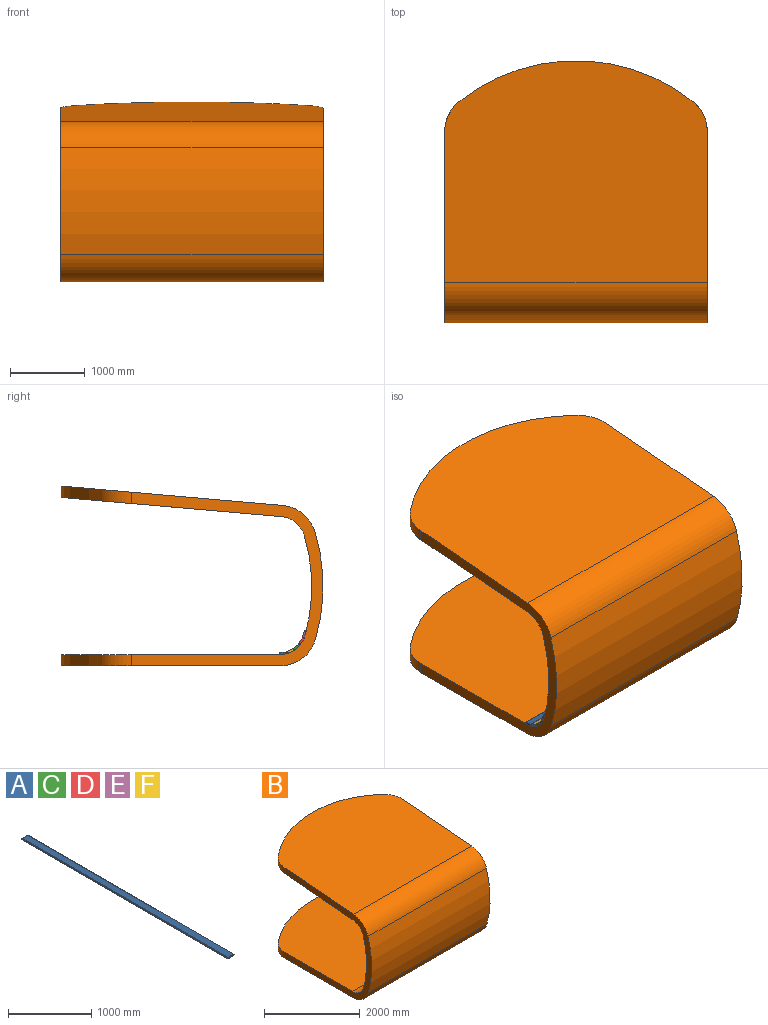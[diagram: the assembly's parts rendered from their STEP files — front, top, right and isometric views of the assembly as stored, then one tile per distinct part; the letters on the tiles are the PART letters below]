
ASSEMBLY  parts=6 mates=9
PART A: 14 faces, bbox 105x3500x25 mm
  f0: plane 3500x91mm, normal (0,0,1), area 318500mm2, adj f8,f9,f11,f13
  f1: plane 3500x1.84mm, normal (-1,0,0), area 6439.1mm2, adj f2,f8,f9,f13
  f2: cylinder r=10mm len=3500mm, axis (0,1,0), area 73303.8mm2, adj f1,f3,f8,f9
  f3: plane 3500x1.84mm, normal (-1,0,0), area 6439.1mm2, adj f2,f8,f9,f12
  f4: plane 3500x91mm, normal (0,0,-1), area 318500mm2, adj f8,f9,f10,f12
  f5: plane 3500x0.5mm, normal (1,0,0), area 1750mm2, adj f6,f8,f9,f10
  f6: cylinder r=10mm len=3500mm, axis (0,1,0), area 109955.7mm2, adj f5,f7,f8,f9
  f7: plane 3500x0.5mm, normal (1,0,0), area 1750mm2, adj f6,f8,f9,f11
  f8: plane 105x25mm, normal (0,-1,0), area 2462.7mm2, adj f0,f1,f2,f3,f4,f5,f6,f7
  f9: plane 105x25mm, normal (0,1,0), area 2462.7mm2, adj f0,f1,f2,f3,f4,f5,f6,f7
  f10: plane 3500x2mm, normal (0.71,0,-0.71), area 9899.5mm2, adj f4,f5,f8,f9
  f11: plane 3500x2mm, normal (0.71,0,0.71), area 9899.5mm2, adj f0,f7,f8,f9
  f12: plane 3500x2mm, normal (-0.71,0,-0.71), area 9899.5mm2, adj f3,f4,f8,f9
  f13: plane 3500x2mm, normal (-0.71,0,0.71), area 9899.5mm2, adj f0,f1,f8,f9
PART B: 18 faces, bbox 3500x3500x2400.1 mm
  f0: plane 3500x2920.83mm, normal (0,0,1), area 9429197.4mm2, adj f3,f10,f11,f13,f14,f15
  f1: plane 3500x2942.68mm, normal (0,0.09,-1), area 9541997.5mm2, adj f5,f10,f11,f12,f16,f17
  f2: plane 3500x2955.76mm, normal (0,-0.09,1), area 9587929mm2, adj f6,f10,f11,f12,f16,f17
  f3: cylinder r=350mm len=3500mm, axis (-1,0,0), area 1578393.4mm2, adj f0,f4,f10,f11
  f4: cylinder r=2350mm len=3500mm, axis (-1,0,0), area 4768488.8mm2, adj f3,f5,f10,f11
  f5: cylinder r=350mm len=3500mm, axis (-1,0,0), area 1452955.7mm2, adj f1,f4,f10,f11
  f6: cylinder r=500mm len=3500mm, axis (-1,0,0), area 2075651mm2, adj f2,f7,f10,f11
  f7: cylinder r=2500mm len=3500mm, axis (-1,0,0), area 5072860.5mm2, adj f6,f8,f10,f11
  f8: cylinder r=500mm len=3500mm, axis (-1,0,0), area 2254847.8mm2, adj f7,f9,f10,f11
  f9: plane 3500x2920.83mm, normal (0,0,-1), area 9429197.4mm2, adj f8,f10,f11,f13,f14,f15
  f10: plane 2561.25x2317.87mm, normal (1,0,0), area 968673.8mm2, adj f0,f1,f2,f3,f4,f5,f6,f7
  f11: plane 2561.25x2317.87mm, normal (-1,0,0), area 968673.8mm2, adj f0,f1,f2,f3,f4,f5,f6,f7
  f12: cylinder r=2500mm len=3125mm, axis (0,0,-1), area 508282.8mm2, adj f1,f2,f16,f17
  f13: cylinder r=2500mm len=3125mm, axis (0,0,-1), area 506348.6mm2, adj f0,f9,f14,f15
  f14: cylinder r=500mm len=390.31mm, axis (0,0,-1), area 67174.9mm2, adj f0,f9,f10,f13
  f15: cylinder r=500mm len=390.31mm, axis (0,0,-1), area 67174.9mm2, adj f0,f9,f11,f13
  f16: cylinder r=500mm len=390.31mm, axis (0,0,-1), area 67431.5mm2, adj f1,f2,f11,f12
  f17: cylinder r=500mm len=390.31mm, axis (0,0,-1), area 67431.5mm2, adj f1,f2,f10,f12
PART C: same geometry as A
PART D: same geometry as A
PART E: same geometry as A
PART F: same geometry as A
PLACE A rot(axis=(-0.07,-0.07,-1),90.3deg) t=(1750,298.72,168.64)mm
PLACE B at identity fixed
PLACE C rot(axis=(-0.33,-0.33,-0.88),97.2deg) t=(1750,121.33,251.37)mm
PLACE D rot(axis=(-0.44,-0.44,-0.78),103.8deg) t=(1750,58.34,327.62)mm
PLACE E rot(axis=(-0.51,-0.51,-0.69),110.8deg) t=(1750,18.27,418.36)mm
PLACE F rot(axis=(-0.21,-0.21,-0.96),92.6deg) t=(1750,203.88,196.91)mm
MATE revolute E.f2 <-> D.f6  axis (1,0,0) through (0,33.54,368.13)mm
MATE cylindrical F.f2 <-> A.f6  axis (1,0,0) through (0,251.67,175.16)mm
MATE cylindrical C.f2 <-> F.f6  axis (1,0,0) through (0,160.65,216.58)mm
MATE planar E.f9 <-> D.f9  axis (1,0,0) through (1750,43.46,378.46)mm
MATE planar D.f9 <-> C.f9  axis (1,0,0) through (1750,56.03,331.4)mm
MATE cylindrical D.f2 <-> C.f6  axis (1,0,0) through (0,85.76,282.85)mm
MATE planar A.f9 <-> B.f10  axis (1,0,0) through (1750,294.33,169.25)mm
MATE planar C.f9 <-> F.f6  axis (1,0,0) through (1750,118.01,254.31)mm
MATE planar F.f9 <-> A.f9  axis (1,0,0) through (1750,199.85,198.74)mm
